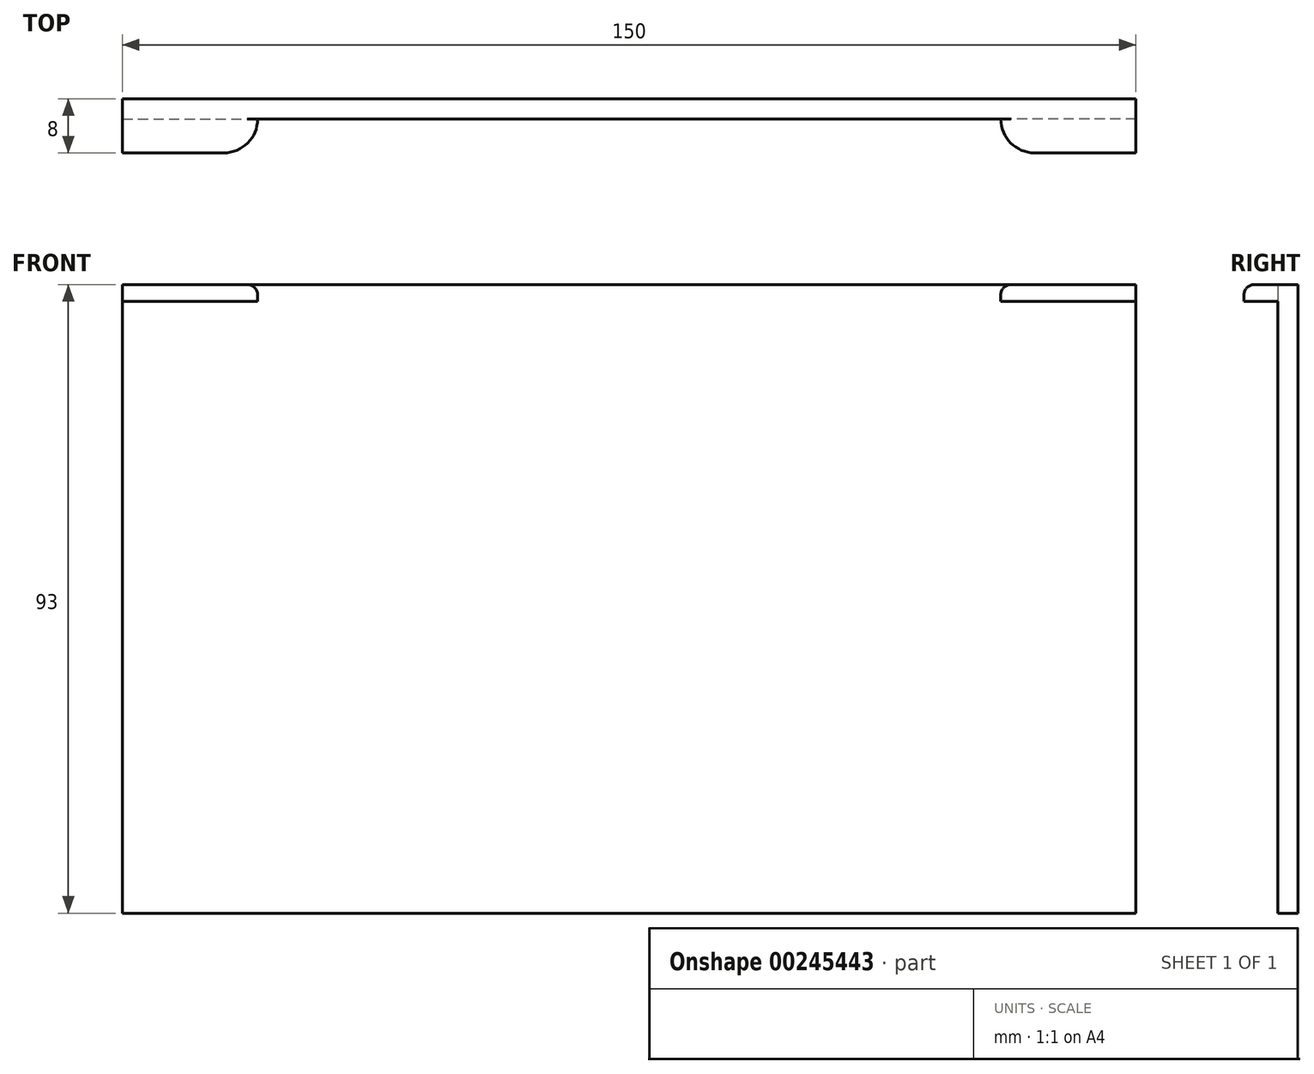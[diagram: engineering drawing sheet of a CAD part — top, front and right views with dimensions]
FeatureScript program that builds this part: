
annotation { "Feature Type Name" : "Feature", "Feature Type Description" : "" }
export const myFeature = defineFeature(function(context is Context, id is Id, definition is map)
    precondition{}
    {
        {
            var Q0;
            Q0=qCreatedBy(makeId("Front.planeOp"),FACE);
            var sketch = newSketch(context, id + "F0", { "sketchPlane" : qUnion([Q0])});
            skLineSegment(sketch, "E0.bottom", {"start": v(0, 0) * mm, "end": v(150, 0) * mm});
            skLineSegment(sketch, "E0.top", {"start": v(0, 93) * mm, "end": v(150, 93) * mm});
            skLineSegment(sketch, "E0.left", {"start": v(0, 0) * mm, "end": v(0, 93) * mm});
            skLineSegment(sketch, "E0.right", {"start": v(150, 0) * mm, "end": v(150, 93) * mm});
            skSolve(sketch);
        }
        {
            var Q0;
            Q0 = qSketchRegion(id + "F0", true);
            extrude(context, id + "F1", {"entities" : qUnion([Q0]), "depth" : 3 * mm});
        }
        {
            var Q0;
            Q0=makeQuery(id+"F1.opExtrude","CAP_FACE",FACE,{"disambiguationData":[OSD([sQuery(id+"F0.wireOp",EDGE,"E0.bottom"),sQuery(id+"F0.wireOp",EDGE,"E0.top"),sQuery(id+"F0.wireOp",EDGE,"E0.left"),sQuery(id+"F0.wireOp",EDGE,"E0.right")])],"isStart":false});
            var sketch = newSketch(context, id + "F2", { "sketchPlane" : qUnion([Q0])});
            skLineSegment(sketch, "E1.bottom", {"start": v(0, 93) * mm, "end": v(20, 93) * mm});
            skLineSegment(sketch, "E1.top", {"start": v(0, 90.5) * mm, "end": v(20, 90.5) * mm});
            skLineSegment(sketch, "E1.left", {"start": v(0, 93) * mm, "end": v(0, 90.5) * mm});
            skLineSegment(sketch, "E1.right", {"start": v(20, 93) * mm, "end": v(20, 90.5) * mm});
            skLineSegment(sketch, "E2.MirrorCS", {"start": v(150, 93) * mm, "end": v(130, 93) * mm});
            skLineSegment(sketch, "E3.MirrorCS", {"start": v(150, 90.5) * mm, "end": v(130, 90.5) * mm});
            skLineSegment(sketch, "E4.MirrorCS", {"start": v(150, 93) * mm, "end": v(150, 90.5) * mm});
            skLineSegment(sketch, "E5.MirrorCS", {"start": v(130, 93) * mm, "end": v(130, 90.5) * mm});
            skSolve(sketch);
        }
        {
            var Q0;
            Q0 = qSketchRegion(id + "F2", true);
            extrude(context, id + "F3", {"entities" : qUnion([Q0]), "operationType" : NewBodyOperationType.ADD, "depth" : 5 * mm});
        }
        {
            var Q0;
            Q0=makeQuery(id+"F3.opExtrude","CAP_EDGE",EDGE,{"disambiguationData":[OSD([sQuery(id+"F2.wireOp",EDGE,"E1.right")])],"isStart":false});
            var Q1;
            Q1=makeQuery(id+"F3.opExtrude","CAP_EDGE",EDGE,{"disambiguationData":[OSD([sQuery(id+"F2.wireOp",EDGE,"E5.MirrorCS")])],"isStart":false});
            fillet(context, id + "F4", {"entities" : qUnion([Q0, Q1]), "radius" : 5 * mm, "tangentPropagation" : true, "allowEdgeOverflow" : false});
        }
        {
            var Q0;
            Q0=makeQuery(id+"F3.opExtrude","CAP_EDGE",EDGE,{"disambiguationData":[OSD([sQuery(id+"F2.wireOp",EDGE,"E1.bottom")])],"isStart":false});
            var Q1;
            Q1=makeQuery(id+"F3.opExtrude","CAP_EDGE",EDGE,{"disambiguationData":[OSD([sQuery(id+"F2.wireOp",EDGE,"E2.MirrorCS")])],"isStart":false});
            fillet(context, id + "F5", {"entities" : qUnion([Q0, Q1]), "radius" : 1.5 * mm, "tangentPropagation" : true, "allowEdgeOverflow" : false});
        }
    });
